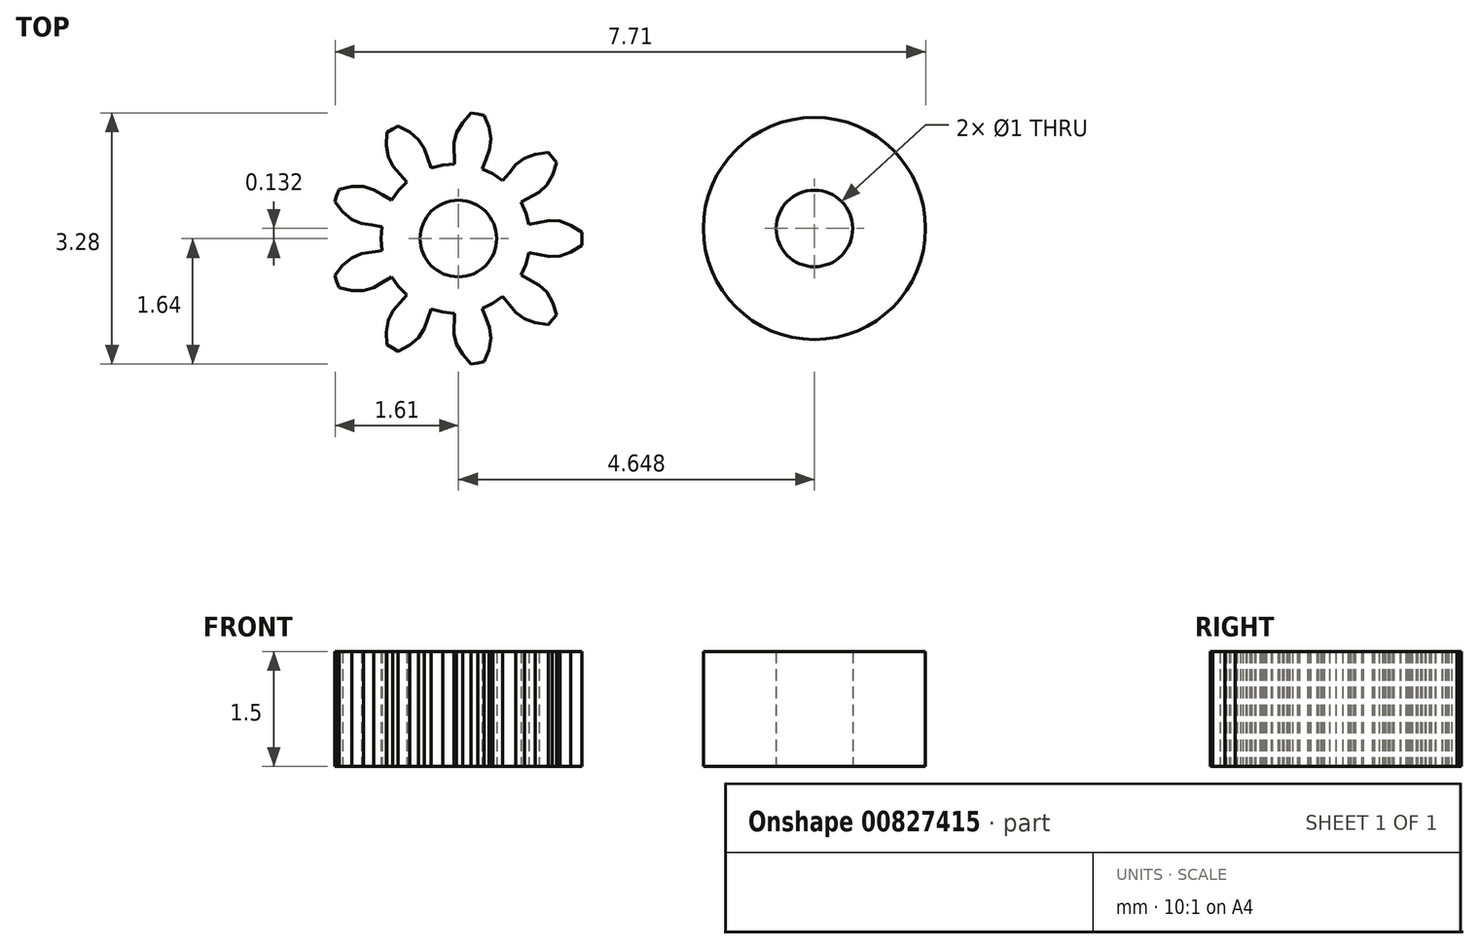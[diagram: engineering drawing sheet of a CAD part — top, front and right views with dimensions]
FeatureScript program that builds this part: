
annotation { "Feature Type Name" : "Feature", "Feature Type Description" : "" }
export const myFeature = defineFeature(function(context is Context, id is Id, definition is map)
    precondition{}
    {
        {
            var Q0;
            Q0=qCreatedBy(makeId("Top.planeOp"),FACE);
            var sketch = newSketch(context, id + "F0", { "sketchPlane" : qUnion([Q0])});
            skLineSegment(sketch, "E0", {"start": v(0.88, -0.33) * mm, "end": v(0.92, -0.18) * mm});
            skLineSegment(sketch, "E1", {"start": v(0.92, -0.18) * mm, "end": v(1.05, -0.2) * mm});
            skLineSegment(sketch, "E2", {"start": v(1.05, -0.2) * mm, "end": v(1.19, -0.23) * mm});
            skLineSegment(sketch, "E3", {"start": v(1.19, -0.23) * mm, "end": v(1.32, -0.23) * mm});
            skLineSegment(sketch, "E4", {"start": v(1.32, -0.23) * mm, "end": v(1.47, -0.17) * mm});
            skLineSegment(sketch, "E5", {"start": v(1.47, -0.17) * mm, "end": v(1.61, -0.08) * mm});
            skLineSegment(sketch, "E6", {"start": v(1.61, -0.08) * mm, "end": v(1.61, 0) * mm});
            skLineSegment(sketch, "E7", {"start": v(1.61, 0) * mm, "end": v(1.61, 0.08) * mm});
            skLineSegment(sketch, "E8", {"start": v(1.61, 0.08) * mm, "end": v(1.47, 0.17) * mm});
            skLineSegment(sketch, "E9", {"start": v(1.47, 0.17) * mm, "end": v(1.32, 0.23) * mm});
            skLineSegment(sketch, "E10", {"start": v(1.32, 0.23) * mm, "end": v(1.19, 0.23) * mm});
            skLineSegment(sketch, "E11", {"start": v(1.19, 0.23) * mm, "end": v(1.05, 0.2) * mm});
            skLineSegment(sketch, "E12", {"start": v(1.05, 0.2) * mm, "end": v(0.92, 0.18) * mm});
            skLineSegment(sketch, "E13", {"start": v(0.92, 0.18) * mm, "end": v(0.88, 0.33) * mm});
            skLineSegment(sketch, "E14", {"start": v(0.88, 0.33) * mm, "end": v(0.82, 0.47) * mm});
            skLineSegment(sketch, "E15", {"start": v(0.82, 0.47) * mm, "end": v(0.93, 0.54) * mm});
            skLineSegment(sketch, "E16", {"start": v(0.93, 0.54) * mm, "end": v(1.05, 0.6) * mm});
            skLineSegment(sketch, "E17", {"start": v(1.05, 0.6) * mm, "end": v(1.15, 0.7) * mm});
            skLineSegment(sketch, "E18", {"start": v(1.15, 0.7) * mm, "end": v(1.23, 0.83) * mm});
            skLineSegment(sketch, "E19", {"start": v(1.23, 0.83) * mm, "end": v(1.28, 1) * mm});
            skLineSegment(sketch, "E20", {"start": v(1.28, 1) * mm, "end": v(1.23, 1.06) * mm});
            skLineSegment(sketch, "E21", {"start": v(1.23, 1.06) * mm, "end": v(1.17, 1.12) * mm});
            skLineSegment(sketch, "E22", {"start": v(1.17, 1.12) * mm, "end": v(1, 1.1) * mm});
            skLineSegment(sketch, "E23", {"start": v(1, 1.1) * mm, "end": v(0.86, 1.05) * mm});
            skLineSegment(sketch, "E24", {"start": v(0.86, 1.05) * mm, "end": v(0.75, 0.97) * mm});
            skLineSegment(sketch, "E25", {"start": v(0.75, 0.97) * mm, "end": v(0.66, 0.86) * mm});
            skLineSegment(sketch, "E26", {"start": v(0.66, 0.86) * mm, "end": v(0.58, 0.76) * mm});
            skLineSegment(sketch, "E27", {"start": v(0.58, 0.76) * mm, "end": v(0.45, 0.84) * mm});
            skLineSegment(sketch, "E28", {"start": v(0.45, 0.84) * mm, "end": v(0.31, 0.91) * mm});
            skLineSegment(sketch, "E29", {"start": v(0.31, 0.91) * mm, "end": v(0.36, 1.04) * mm});
            skLineSegment(sketch, "E30", {"start": v(0.36, 1.04) * mm, "end": v(0.4, 1.16) * mm});
            skLineSegment(sketch, "E31", {"start": v(0.4, 1.16) * mm, "end": v(0.42, 1.3) * mm});
            skLineSegment(sketch, "E32", {"start": v(0.42, 1.3) * mm, "end": v(0.4, 1.45) * mm});
            skLineSegment(sketch, "E33", {"start": v(0.4, 1.45) * mm, "end": v(0.33, 1.6) * mm});
            skLineSegment(sketch, "E34", {"start": v(0.33, 1.6) * mm, "end": v(0.25, 1.62) * mm});
            skLineSegment(sketch, "E35", {"start": v(0.25, 1.62) * mm, "end": v(0.17, 1.64) * mm});
            skLineSegment(sketch, "E36", {"start": v(0.17, 1.64) * mm, "end": v(0.05, 1.51) * mm});
            skLineSegment(sketch, "E37", {"start": v(0.05, 1.51) * mm, "end": v(-0.02, 1.38) * mm});
            skLineSegment(sketch, "E38", {"start": v(-0.02, 1.38) * mm, "end": v(-0.05, 1.24) * mm});
            skLineSegment(sketch, "E39", {"start": v(-0.05, 1.24) * mm, "end": v(-0.05, 1.1) * mm});
            skLineSegment(sketch, "E40", {"start": v(-0.05, 1.1) * mm, "end": v(-0.05, 0.97) * mm});
            skLineSegment(sketch, "E41", {"start": v(-0.05, 0.97) * mm, "end": v(-0.2, 0.96) * mm});
            skLineSegment(sketch, "E42", {"start": v(-0.2, 0.96) * mm, "end": v(-0.36, 0.92) * mm});
            skLineSegment(sketch, "E43", {"start": v(-0.36, 0.92) * mm, "end": v(-0.4, 1.05) * mm});
            skLineSegment(sketch, "E44", {"start": v(-0.4, 1.05) * mm, "end": v(-0.44, 1.18) * mm});
            skLineSegment(sketch, "E45", {"start": v(-0.44, 1.18) * mm, "end": v(-0.52, 1.3) * mm});
            skLineSegment(sketch, "E46", {"start": v(-0.52, 1.3) * mm, "end": v(-0.64, 1.4) * mm});
            skLineSegment(sketch, "E47", {"start": v(-0.64, 1.4) * mm, "end": v(-0.79, 1.47) * mm});
            skLineSegment(sketch, "E48", {"start": v(-0.79, 1.47) * mm, "end": v(-0.86, 1.43) * mm});
            skLineSegment(sketch, "E49", {"start": v(-0.86, 1.43) * mm, "end": v(-0.93, 1.38) * mm});
            skLineSegment(sketch, "E50", {"start": v(-0.93, 1.38) * mm, "end": v(-0.94, 1.22) * mm});
            skLineSegment(sketch, "E51", {"start": v(-0.94, 1.22) * mm, "end": v(-0.91, 1.06) * mm});
            skLineSegment(sketch, "E52", {"start": v(-0.91, 1.06) * mm, "end": v(-0.85, 0.94) * mm});
            skLineSegment(sketch, "E53", {"start": v(-0.85, 0.94) * mm, "end": v(-0.76, 0.84) * mm});
            skLineSegment(sketch, "E54", {"start": v(-0.76, 0.84) * mm, "end": v(-0.67, 0.74) * mm});
            skLineSegment(sketch, "E55", {"start": v(-0.67, 0.74) * mm, "end": v(-0.78, 0.63) * mm});
            skLineSegment(sketch, "E56", {"start": v(-0.78, 0.63) * mm, "end": v(-0.87, 0.5) * mm});
            skLineSegment(sketch, "E57", {"start": v(-0.87, 0.5) * mm, "end": v(-0.99, 0.57) * mm});
            skLineSegment(sketch, "E58", {"start": v(-0.99, 0.57) * mm, "end": v(-1.1, 0.64) * mm});
            skLineSegment(sketch, "E59", {"start": v(-1.1, 0.64) * mm, "end": v(-1.24, 0.68) * mm});
            skLineSegment(sketch, "E60", {"start": v(-1.24, 0.68) * mm, "end": v(-1.4, 0.68) * mm});
            skLineSegment(sketch, "E61", {"start": v(-1.4, 0.68) * mm, "end": v(-1.56, 0.64) * mm});
            skLineSegment(sketch, "E62", {"start": v(-1.56, 0.64) * mm, "end": v(-1.59, 0.56) * mm});
            skLineSegment(sketch, "E63", {"start": v(-1.59, 0.56) * mm, "end": v(-1.61, 0.48) * mm});
            skLineSegment(sketch, "E64", {"start": v(-1.61, 0.48) * mm, "end": v(-1.5, 0.35) * mm});
            skLineSegment(sketch, "E65", {"start": v(-1.5, 0.35) * mm, "end": v(-1.4, 0.25) * mm});
            skLineSegment(sketch, "E66", {"start": v(-1.4, 0.25) * mm, "end": v(-1.27, 0.2) * mm});
            skLineSegment(sketch, "E67", {"start": v(-1.27, 0.2) * mm, "end": v(-1.13, 0.18) * mm});
            skLineSegment(sketch, "E68", {"start": v(-1.13, 0.18) * mm, "end": v(-1, 0.15) * mm});
            skLineSegment(sketch, "E69", {"start": v(-1, 0.15) * mm, "end": v(-1.01, 0) * mm});
            skLineSegment(sketch, "E70", {"start": v(-1.01, 0) * mm, "end": v(-1, -0.15) * mm});
            skLineSegment(sketch, "E71", {"start": v(-1, -0.15) * mm, "end": v(-1.13, -0.18) * mm});
            skLineSegment(sketch, "E72", {"start": v(-1.13, -0.18) * mm, "end": v(-1.27, -0.2) * mm});
            skLineSegment(sketch, "E73", {"start": v(-1.27, -0.2) * mm, "end": v(-1.4, -0.25) * mm});
            skLineSegment(sketch, "E74", {"start": v(-1.4, -0.25) * mm, "end": v(-1.5, -0.35) * mm});
            skLineSegment(sketch, "E75", {"start": v(-1.5, -0.35) * mm, "end": v(-1.61, -0.48) * mm});
            skLineSegment(sketch, "E76", {"start": v(-1.61, -0.48) * mm, "end": v(-1.59, -0.56) * mm});
            skLineSegment(sketch, "E77", {"start": v(-1.59, -0.56) * mm, "end": v(-1.56, -0.64) * mm});
            skLineSegment(sketch, "E78", {"start": v(-1.56, -0.64) * mm, "end": v(-1.4, -0.68) * mm});
            skLineSegment(sketch, "E79", {"start": v(-1.4, -0.68) * mm, "end": v(-1.24, -0.68) * mm});
            skLineSegment(sketch, "E80", {"start": v(-1.24, -0.68) * mm, "end": v(-1.1, -0.64) * mm});
            skLineSegment(sketch, "E81", {"start": v(-1.1, -0.64) * mm, "end": v(-0.99, -0.57) * mm});
            skLineSegment(sketch, "E82", {"start": v(-0.99, -0.57) * mm, "end": v(-0.87, -0.5) * mm});
            skLineSegment(sketch, "E83", {"start": v(-0.87, -0.5) * mm, "end": v(-0.78, -0.63) * mm});
            skLineSegment(sketch, "E84", {"start": v(-0.78, -0.63) * mm, "end": v(-0.67, -0.74) * mm});
            skLineSegment(sketch, "E85", {"start": v(-0.67, -0.74) * mm, "end": v(-0.76, -0.84) * mm});
            skLineSegment(sketch, "E86", {"start": v(-0.76, -0.84) * mm, "end": v(-0.85, -0.94) * mm});
            skLineSegment(sketch, "E87", {"start": v(-0.85, -0.94) * mm, "end": v(-0.91, -1.06) * mm});
            skLineSegment(sketch, "E88", {"start": v(-0.91, -1.06) * mm, "end": v(-0.94, -1.22) * mm});
            skLineSegment(sketch, "E89", {"start": v(-0.94, -1.22) * mm, "end": v(-0.93, -1.38) * mm});
            skLineSegment(sketch, "E90", {"start": v(-0.93, -1.38) * mm, "end": v(-0.86, -1.43) * mm});
            skLineSegment(sketch, "E91", {"start": v(-0.86, -1.43) * mm, "end": v(-0.79, -1.47) * mm});
            skLineSegment(sketch, "E92", {"start": v(-0.79, -1.47) * mm, "end": v(-0.64, -1.4) * mm});
            skLineSegment(sketch, "E93", {"start": v(-0.64, -1.4) * mm, "end": v(-0.52, -1.3) * mm});
            skLineSegment(sketch, "E94", {"start": v(-0.52, -1.3) * mm, "end": v(-0.44, -1.18) * mm});
            skLineSegment(sketch, "E95", {"start": v(-0.44, -1.18) * mm, "end": v(-0.4, -1.05) * mm});
            skLineSegment(sketch, "E96", {"start": v(-0.4, -1.05) * mm, "end": v(-0.36, -0.92) * mm});
            skLineSegment(sketch, "E97", {"start": v(-0.36, -0.92) * mm, "end": v(-0.2, -0.96) * mm});
            skLineSegment(sketch, "E98", {"start": v(-0.2, -0.96) * mm, "end": v(-0.05, -0.97) * mm});
            skLineSegment(sketch, "E99", {"start": v(-0.05, -0.97) * mm, "end": v(-0.05, -1.1) * mm});
            skLineSegment(sketch, "E100", {"start": v(-0.05, -1.1) * mm, "end": v(-0.05, -1.24) * mm});
            skLineSegment(sketch, "E101", {"start": v(-0.05, -1.24) * mm, "end": v(-0.02, -1.38) * mm});
            skLineSegment(sketch, "E102", {"start": v(-0.02, -1.38) * mm, "end": v(0.05, -1.51) * mm});
            skLineSegment(sketch, "E103", {"start": v(0.05, -1.51) * mm, "end": v(0.17, -1.64) * mm});
            skLineSegment(sketch, "E104", {"start": v(0.17, -1.64) * mm, "end": v(0.25, -1.62) * mm});
            skLineSegment(sketch, "E105", {"start": v(0.25, -1.62) * mm, "end": v(0.33, -1.6) * mm});
            skLineSegment(sketch, "E106", {"start": v(0.33, -1.6) * mm, "end": v(0.4, -1.45) * mm});
            skLineSegment(sketch, "E107", {"start": v(0.4, -1.45) * mm, "end": v(0.42, -1.3) * mm});
            skLineSegment(sketch, "E108", {"start": v(0.42, -1.3) * mm, "end": v(0.4, -1.16) * mm});
            skLineSegment(sketch, "E109", {"start": v(0.4, -1.16) * mm, "end": v(0.36, -1.04) * mm});
            skLineSegment(sketch, "E110", {"start": v(0.36, -1.04) * mm, "end": v(0.31, -0.91) * mm});
            skLineSegment(sketch, "E111", {"start": v(0.31, -0.91) * mm, "end": v(0.45, -0.84) * mm});
            skLineSegment(sketch, "E112", {"start": v(0.45, -0.84) * mm, "end": v(0.58, -0.76) * mm});
            skLineSegment(sketch, "E113", {"start": v(0.58, -0.76) * mm, "end": v(0.66, -0.86) * mm});
            skLineSegment(sketch, "E114", {"start": v(0.66, -0.86) * mm, "end": v(0.75, -0.97) * mm});
            skLineSegment(sketch, "E115", {"start": v(0.75, -0.97) * mm, "end": v(0.86, -1.05) * mm});
            skLineSegment(sketch, "E116", {"start": v(0.86, -1.05) * mm, "end": v(1, -1.1) * mm});
            skLineSegment(sketch, "E117", {"start": v(1, -1.1) * mm, "end": v(1.17, -1.12) * mm});
            skLineSegment(sketch, "E118", {"start": v(1.17, -1.12) * mm, "end": v(1.23, -1.06) * mm});
            skLineSegment(sketch, "E119", {"start": v(1.23, -1.06) * mm, "end": v(1.28, -1) * mm});
            skLineSegment(sketch, "E120", {"start": v(1.28, -1) * mm, "end": v(1.23, -0.83) * mm});
            skLineSegment(sketch, "E121", {"start": v(1.23, -0.83) * mm, "end": v(1.15, -0.7) * mm});
            skLineSegment(sketch, "E122", {"start": v(1.15, -0.7) * mm, "end": v(1.05, -0.6) * mm});
            skLineSegment(sketch, "E123", {"start": v(1.05, -0.6) * mm, "end": v(0.93, -0.54) * mm});
            skLineSegment(sketch, "E124", {"start": v(0.93, -0.54) * mm, "end": v(0.82, -0.47) * mm});
            skLineSegment(sketch, "E125", {"start": v(0.88, -0.33) * mm, "end": v(0.82, -0.47) * mm});
            skCircle(sketch, "E126", {"center": v(0, 0) * mm, "radius": 0.5 * mm});
            skSolve(sketch);
        }
        {
            var Q0;
            Q0=makeQuery(id+"F0.imprint","IMPRINT",FACE,{"disambiguationData":[TD([[makeQuery(id+"F0.imprint","IMPRINT",EDGE,{"derivedFrom":sQuery(id+"F0.wireOp",EDGE,"E0")}),1.0]])]});
            extrude(context, id + "F1", {"entities" : qUnion([Q0]), "depth" : 1.5 * mm, "offsetDistance" : 25 * mm});
        }
        {
            var Q0;
            Q0=qCreatedBy(makeId("Top.planeOp"),FACE);
            var sketch = newSketch(context, id + "F2", { "sketchPlane" : qUnion([Q0])});
            skCircle(sketch, "E127", {"center": v(4.65, 0.13) * mm, "radius": 1.45 * mm});
            skCircle(sketch, "E128", {"center": v(4.65, 0.13) * mm, "radius": 0.5 * mm});
            skSolve(sketch);
        }
        {
            var Q0;
            Q0 = qSketchRegion(id + "F2", true);
            extrude(context, id + "F3", {"entities" : qUnion([Q0]), "depth" : 1.5 * mm, "offsetDistance" : 25 * mm});
        }
    });
